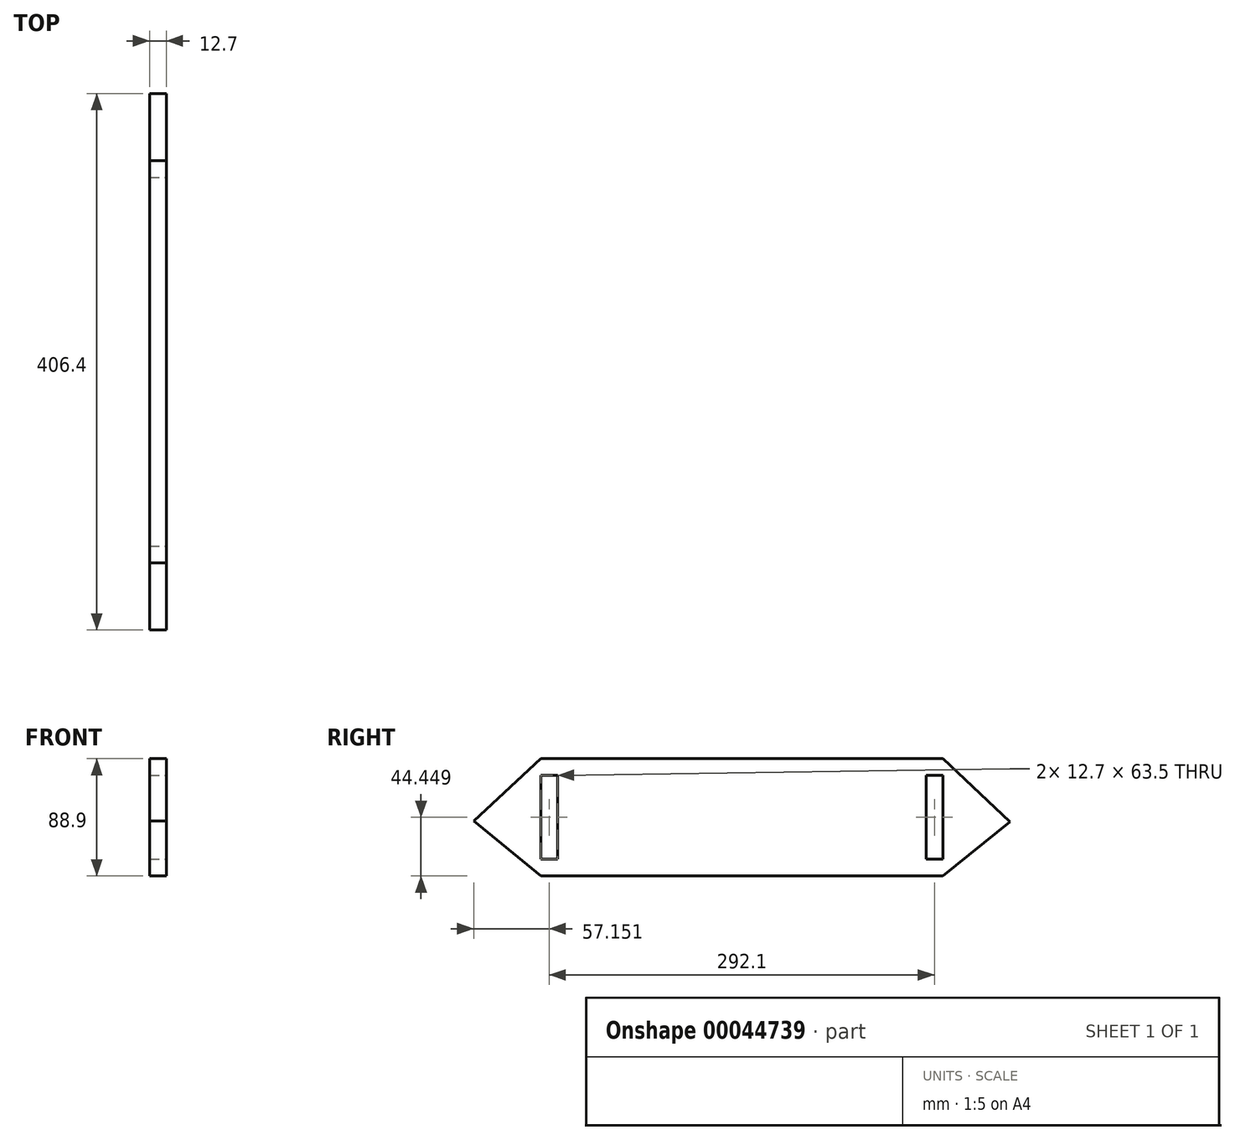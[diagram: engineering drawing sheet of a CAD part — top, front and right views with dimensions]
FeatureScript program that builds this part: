
annotation { "Feature Type Name" : "Feature", "Feature Type Description" : "" }
export const myFeature = defineFeature(function(context is Context, id is Id, definition is map)
    precondition{}
    {
        {
            var Q0;
            Q0=qCreatedBy(makeId("Right.planeOp"),FACE);
            var sketch = newSketch(context, id + "F0", { "sketchPlane" : qUnion([Q0])});
            skLineSegment(sketch, "E0.bottom", {"start": v(-151.82, -53.67) * mm, "end": v(152.98, -53.67) * mm});
            skLineSegment(sketch, "E0.top", {"start": v(-151.82, 35.23) * mm, "end": v(152.98, 35.23) * mm});
            skLineSegment(sketch, "E0.left", {"start": v(-151.82, -53.67) * mm, "end": v(-151.82, 35.23) * mm});
            skLineSegment(sketch, "E0.right", {"start": v(152.98, -53.67) * mm, "end": v(152.98, 35.23) * mm});
            skLineSegment(sketch, "E1", {"start": v(152.98, 35.23) * mm, "end": v(203.78, -12.53) * mm});
            skLineSegment(sketch, "E2", {"start": v(203.78, -12.53) * mm, "end": v(152.98, -53.67) * mm});
            skLineSegment(sketch, "E3", {"start": v(-151.82, 35.23) * mm, "end": v(-202.62, -11.98) * mm});
            skLineSegment(sketch, "E4", {"start": v(-202.62, -11.98) * mm, "end": v(-151.82, -53.67) * mm});
            skSolve(sketch);
        }
        {
            var Q0;
            Q0=qSketchRegion(id+"F0",true);
            extrude(context, id + "F1", {"entities" : qUnion([Q0]), "depth" : 12.7 * mm});
        }
        {
            var Q0;
            Q0=makeQuery(id+"F1.opExtrude","CAP_FACE",FACE,{"disambiguationData":[OSD([sQuery(id+"F0.wireOp",EDGE,"E0.bottom"),sQuery(id+"F0.wireOp",EDGE,"E0.top"),sQuery(id+"F0.wireOp",EDGE,"E1"),sQuery(id+"F0.wireOp",EDGE,"E2"),sQuery(id+"F0.wireOp",EDGE,"E3"),sQuery(id+"F0.wireOp",EDGE,"E4")])],"isStart":false});
            var sketch = newSketch(context, id + "F2", { "sketchPlane" : qUnion([Q0])});
            skLineSegment(sketch, "E5.bottom", {"start": v(-151.82, -40.97) * mm, "end": v(-139.12, -40.97) * mm});
            skLineSegment(sketch, "E5.top", {"start": v(-151.82, 22.53) * mm, "end": v(-139.12, 22.53) * mm});
            skLineSegment(sketch, "E5.left", {"start": v(-151.82, -40.97) * mm, "end": v(-151.82, 22.53) * mm});
            skLineSegment(sketch, "E5.right", {"start": v(-139.12, -40.97) * mm, "end": v(-139.12, 22.53) * mm});
            skLineSegment(sketch, "E6.bottom", {"start": v(152.98, -40.97) * mm, "end": v(140.28, -40.97) * mm});
            skLineSegment(sketch, "E6.top", {"start": v(152.98, 22.53) * mm, "end": v(140.28, 22.53) * mm});
            skLineSegment(sketch, "E6.left", {"start": v(152.98, -40.97) * mm, "end": v(152.98, 22.53) * mm});
            skLineSegment(sketch, "E6.right", {"start": v(140.28, -40.97) * mm, "end": v(140.28, 22.53) * mm});
            skSolve(sketch);
        }
        {
            var Q0;
            Q0=qSketchRegion(id+"F2",true);
            extrude(context, id + "F3", {"entities" : qUnion([Q0]), "operationType" : NewBodyOperationType.REMOVE, "oppositeDirection" : true, "depth" : 12.7 * mm});
        }
    });
